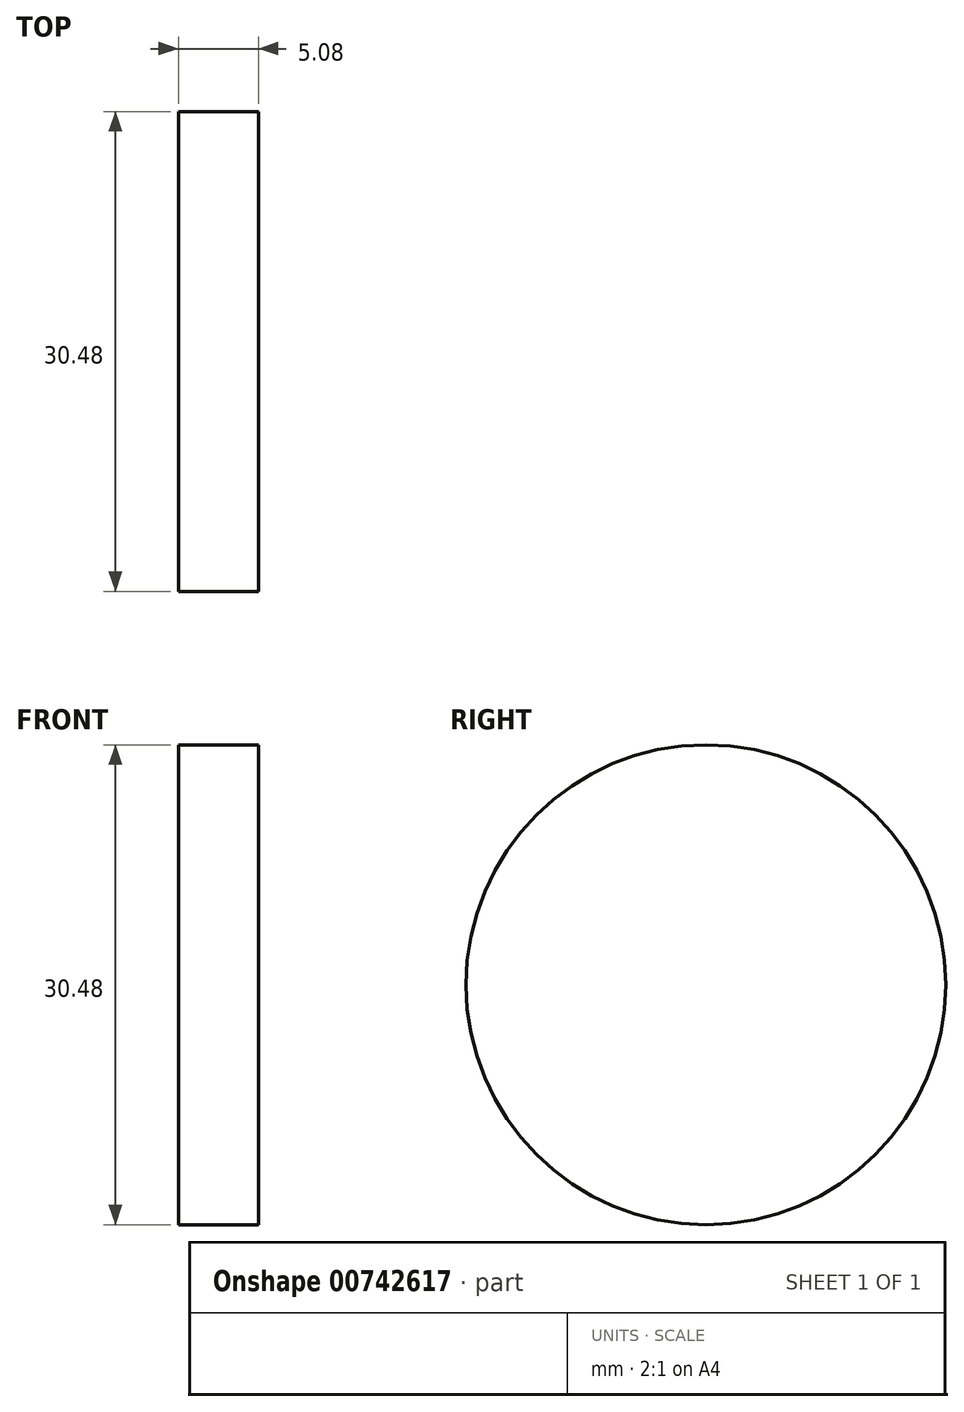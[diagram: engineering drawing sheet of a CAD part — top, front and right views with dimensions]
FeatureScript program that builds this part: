
annotation { "Feature Type Name" : "Feature", "Feature Type Description" : "" }
export const myFeature = defineFeature(function(context is Context, id is Id, definition is map)
    precondition{}
    {
        {
            var Q0;
            Q0=qCreatedBy(makeId("Right.planeOp"),FACE);
            var sketch = newSketch(context, id + "F0", { "sketchPlane" : qUnion([Q0])});
            skCircle(sketch, "E0", {"center": v(0, 0) * mm, "radius": 15.24 * mm});
            skSolve(sketch);
        }
        {
            var Q0;
            Q0 = qSketchRegion(id + "F0", true);
            extrude(context, id + "F1", {"entities" : qUnion([Q0]), "depth" : 5.08 * mm, "offsetDistance" : 25.4 * mm});
        }
    });
